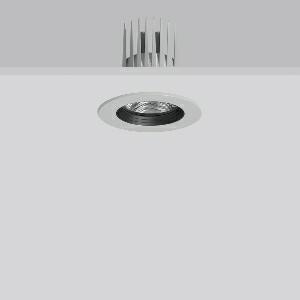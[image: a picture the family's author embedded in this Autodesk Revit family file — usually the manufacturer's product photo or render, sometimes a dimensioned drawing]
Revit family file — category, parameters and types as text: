
# Revit family: heledon_mini_e_901750_004_76_0b19
name_source: partatom
category: Lighting Fixtures
units: mm (PartAtom-declared; Revit-internal decimal feet)

## family parameters
Cut with Voids When Loaded = No
Host = Face
Light Source = No
Part Type = Normal
Room Calculation Point = No
Round Connector Dimension = Use Diameter
Shared = No

## types (1)
- HELEDON mini E (1 x LED Modul 930, 3650 lm, 3000)
    Apparent Load = 29 VA
    Approval mark = CE
    CIE Flux Codes = 95 99 100 100 100
    Color Rendering = 90
    Color Temperature = 3000
    Default Elevation = 1800 mm
    Description = Series: HELEDON mini
Round recessed downlight. Housing: die-cast aluminium, powder-coated. Black plastic ring and recessed LED to prevent glare from the side. Optical assembly with reflector made of MIRO-Silver with 98% total light reflection for outstanding efficiency - can be changed without tools. Best colour rendering index Ra>90. Suitable for Recessed ceiling mounting. Installation without tools thanks to spring fastening system. Including separate LED converter with connecting cable 600 mm.High quality converter without flickering and stroboscopic effect. Through-wiring box (5 pole) available as accessory. The following accessories can be mounted without use of tools: interchangeable lenses, decorative glasses, honeycomb louvre, clear and frosted diffusers, white interchangeable plastic ring. 
Colour: silver
Diameter: 124 mm
Height: 3 mm
Cut-out diameter: 114 mm
Recess height: 170 mm
Luminaire: recess height: 120 mm
Lamp: LED
Socket: without socket
Colour temperature: 3000K
Colour rendering index (CRI): 92
System power: 29 W
Rated luminous flux: 3650 lm
Luminous efficiency: 126 lm/W
Control gear: Converter, dimmable, DALI
Protection class: II
Type of protection: IP 20
    Height = 0 mm  [stored 0 ft]
    Lamp = 1 x LED Modul 930
    Lamp Light Flux = 3650 lm
    Lamp count = 1
    Length = 124 mm  [stored 0.406824 ft]
    Lifetime = 50000 h
    Luminous efficacy = 126 lm/W
    Manufacturer = RZB
    ModVariant = No
    Model = 901750.004.76
    Mounting Place = Ceiling
    Mounting Type = Recessed
    Number of Poles = 1
    OnlyDefault = Yes
    Power Factor = 1
    Product Name = HELEDON mini E
    Product group = Recessed downlights
    ProductGroupID = 402
    Protection Class = Protection class II
    Protection Degree = IP 20
    RLX_Detail_Level = 1
    RLX_Emergency_Light_Flux = 0 lm
    RLX_Emergency_Type = 0
    RLX_Emergency_Type_DB = No
    RlxData = <blob elided: 127017 chars, md5=5b823146>
    Socket = socket
    Standby Power = 0 W
    System Light Flux = 3650 lm
    System Power = 29 W
    Type Comments = Product without accessories
    Type Image = 901657.004.jpg
    URL = http://relux.com
    VarID = ---
    Voltage = 230 V
    Voltage Range = 220-240 V
    Weight = 0.00 kg
    Width = 0 mm  [stored 0 ft]

note: [stored X ft] marks values corroborated as IEEE doubles in the binary element streams (Revit-internal decimal feet)

## geometry (parser evidence)
native form markers: Blend x4, Sweep x12
no freeform markers — native parametric forms only
